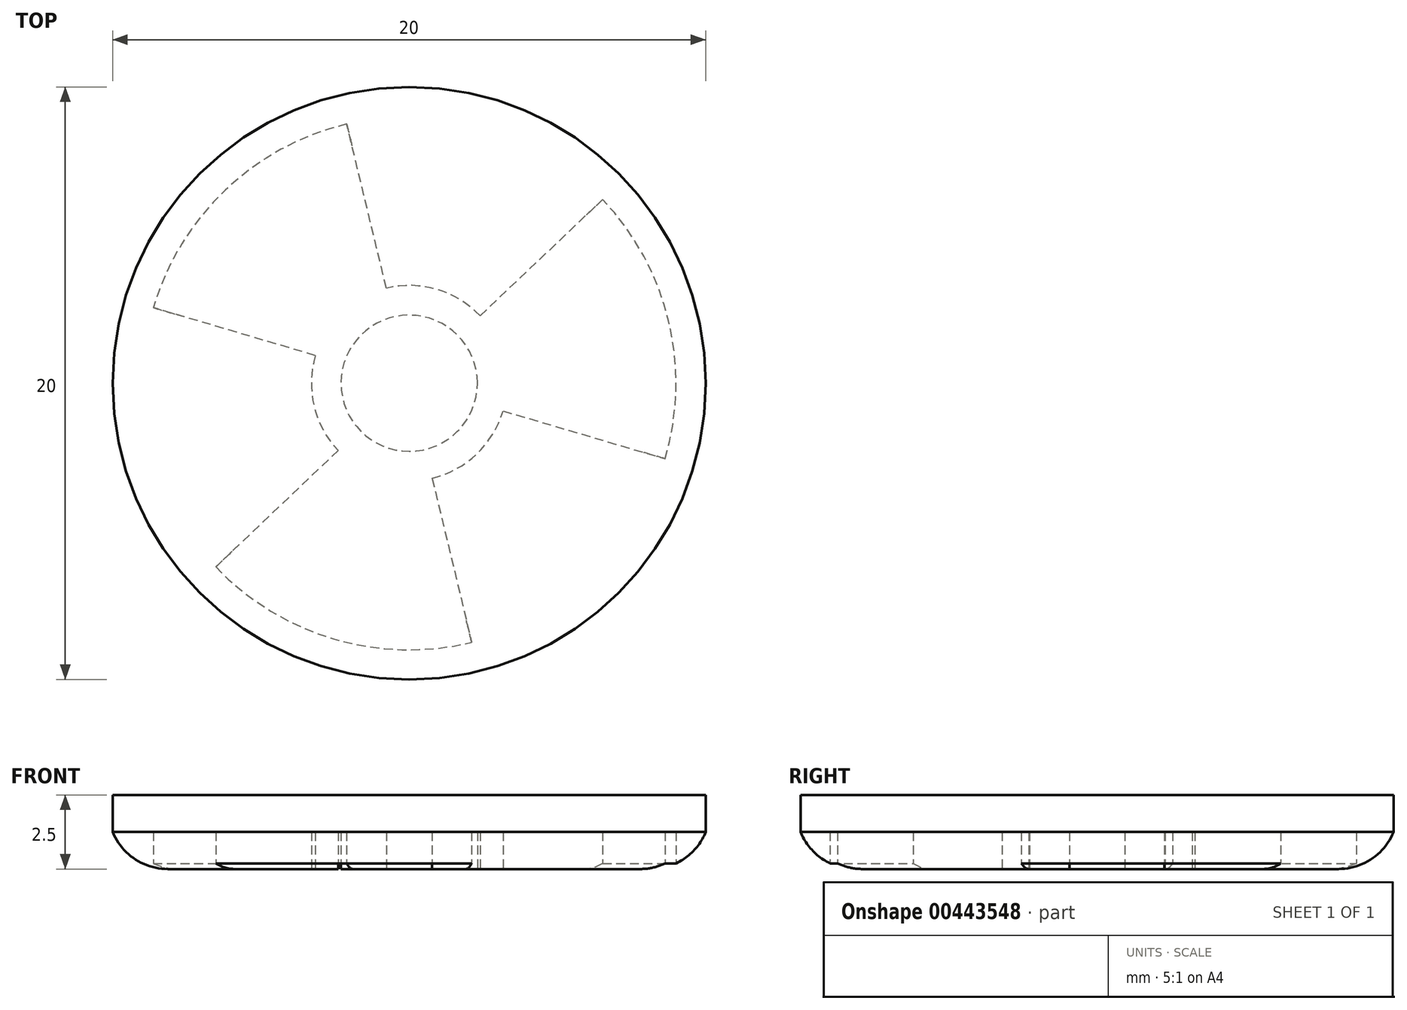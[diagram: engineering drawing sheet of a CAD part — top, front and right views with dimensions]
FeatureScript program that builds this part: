
annotation { "Feature Type Name" : "Feature", "Feature Type Description" : "" }
export const myFeature = defineFeature(function(context is Context, id is Id, definition is map)
    precondition{}
    {
        {
            var Q0;
            Q0=qCreatedBy(makeId("Top.planeOp"),FACE);
            var sketch = newSketch(context, id + "F0", { "sketchPlane" : qUnion([Q0])});
            skCircle(sketch, "E0", {"center": v(0, 0) * mm, "radius": 10 * mm});
            skArc(sketch, "E1", {"start": v(-6.52, -6.2) * mm, "mid": v(-2.55, -8.63) * mm, "end": v(2.1, -8.75) * mm});
            skArc(sketch, "E2", {"start": v(0.77, -3.2) * mm, "mid": v(2.27, -2.4) * mm, "end": v(3.16, -0.93) * mm});
            skCircle(sketch, "E3", {"center": v(0, 0) * mm, "radius": 2.3 * mm});
            skLineSegment(sketch, "E4.trimOffspring", {"start": v(-2.4, -2.27) * mm, "end": v(-6.52, -6.2) * mm});
            skLineSegment(sketch, "E5.trimOffspring", {"start": v(-3.16, 0.93) * mm, "end": v(-8.63, 2.55) * mm});
            skLineSegment(sketch, "E6.trimOffspring", {"start": v(-0.77, 3.2) * mm, "end": v(-2.1, 8.75) * mm});
            skLineSegment(sketch, "E7.trimOffspring", {"start": v(2.4, 2.27) * mm, "end": v(6.52, 6.2) * mm});
            skLineSegment(sketch, "E8.trimOffspring", {"start": v(3.16, -0.93) * mm, "end": v(8.63, -2.55) * mm});
            skLineSegment(sketch, "E9.trimOffspring", {"start": v(0.77, -3.2) * mm, "end": v(2.1, -8.75) * mm});
            skArc(sketch, "E10.trimOffspring", {"start": v(-2.1, 8.75) * mm, "mid": v(-6.2, 6.52) * mm, "end": v(-8.63, 2.55) * mm});
            skArc(sketch, "E11.trimOffspring", {"start": v(8.63, -2.55) * mm, "mid": v(8.75, 2.1) * mm, "end": v(6.52, 6.2) * mm});
            skArc(sketch, "E12.trimOffspring", {"start": v(-3.16, 0.93) * mm, "mid": v(-3.2, -0.77) * mm, "end": v(-2.4, -2.27) * mm});
            skArc(sketch, "E13.trimOffspring", {"start": v(2.4, 2.27) * mm, "mid": v(0.93, 3.16) * mm, "end": v(-0.77, 3.2) * mm});
            skSolve(sketch);
        }
        {
            var Q0;
            Q0=makeQuery(id+"F0.imprint","IMPRINT",FACE,{"disambiguationData":[TD([[makeQuery(id+"F0.imprint","IMPRINT",EDGE,{"derivedFrom":sQuery(id+"F0.wireOp",EDGE,"E3")}),1.0]])]});
            var Q1;
            Q1=makeQuery(id+"F0.imprint","IMPRINT",FACE,{"disambiguationData":[TD([[makeQuery(id+"F0.imprint","IMPRINT",EDGE,{"derivedFrom":sQuery(id+"F0.wireOp",EDGE,"E0")}),1.0]])]});
            extrude(context, id + "F1", {"entities" : qUnion([Q0, Q1]), "depth" : 1.25 * mm});
        }
        {
            var Q0;
            Q0=makeQuery(id+"F1.opExtrude","CAP_EDGE",EDGE,{"disambiguationData":[OSD([sQuery(id+"F0.wireOp",EDGE,"E0")])],"isStart":true});
            fillet(context, id + "F2", {"entities" : qUnion([Q0]), "radius" : 2 * mm, "tangentPropagation" : true, "allowEdgeOverflow" : false});
        }
        {
            var Q0;
            Q0=makeQuery(id+"F0.imprint","IMPRINT",FACE,{"disambiguationData":[TD([[makeQuery(id+"F0.imprint","IMPRINT",EDGE,{"derivedFrom":sQuery(id+"F0.wireOp",EDGE,"E1")}),1.0]])]});
            var Q1;
            Q1=makeQuery(id+"F0.imprint","IMPRINT",FACE,{"disambiguationData":[TD([[makeQuery(id+"F0.imprint","IMPRINT",EDGE,{"derivedFrom":sQuery(id+"F0.wireOp",EDGE,"E0")}),1.0]])]});
            var Q2;
            Q2=makeQuery(id+"F0.imprint","IMPRINT",FACE,{"disambiguationData":[TD([[makeQuery(id+"F0.imprint","IMPRINT",EDGE,{"derivedFrom":sQuery(id+"F0.wireOp",EDGE,"E3")}),1.0]])]});
            extrude(context, id + "F3", {"entities" : qUnion([Q0, Q1, Q2]), "depth" : 2.5 * mm, "hasSecondDirection" : true, "secondDirectionOppositeDirection" : true, "secondDirectionDepth" : -1.25 * mm});
        }
    });
